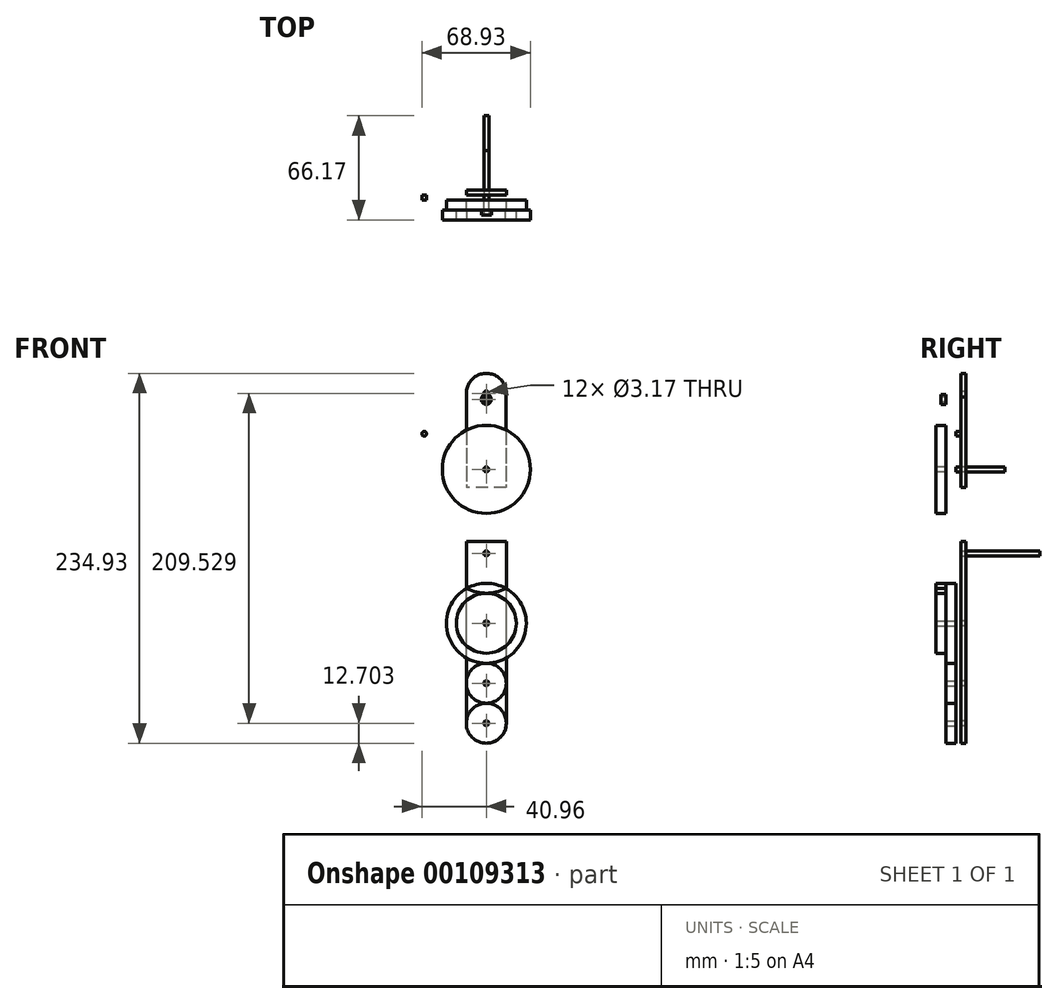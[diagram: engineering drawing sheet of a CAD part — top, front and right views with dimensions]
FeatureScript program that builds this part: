
annotation { "Feature Type Name" : "Feature", "Feature Type Description" : "" }
export const myFeature = defineFeature(function(context is Context, id is Id, definition is map)
    precondition{}
    {
        {
            var Q0;
            Q0=qCreatedBy(makeId("Front.planeOp"),FACE);
            var sketch = newSketch(context, id + "F0", { "sketchPlane" : qUnion([Q0])});
            skLineSegment(sketch, "E0.MirrorCS", {"start": v(12.47, 255.41) * mm, "end": v(42.64, 235.3) * mm});
            skArc(sketch, "E1.MirrorCS", {"start": v(12.47, 255.41) * mm, "mid": v(9.8, 265.9) * mm, "end": v(0, 270.52) * mm});
            skArc(sketch, "E2", {"start": v(-12.7, 48.29) * mm, "mid": v(0, 35.59) * mm, "end": v(12.7, 48.29) * mm});
            skLineSegment(sketch, "E3", {"start": v(12.7, 48.29) * mm, "end": v(42.64, 71.85) * mm});
            skLineSegment(sketch, "E4", {"start": v(42.64, 71.85) * mm, "end": v(42.64, 235.3) * mm});
            skLineSegment(sketch, "E5", {"start": v(-44.4, 144.8) * mm, "end": v(42.64, 144.8) * mm});
            skLineSegment(sketch, "E6", {"start": v(-44.4, 151.14) * mm, "end": v(-44.4, 144.8) * mm});
            skArc(sketch, "E7.MirrorCS", {"start": v(-12.47, 255.41) * mm, "mid": v(-9.8, 265.9) * mm, "end": v(0, 270.52) * mm});
            skLineSegment(sketch, "E8.MirrorCS", {"start": v(-12.47, 255.41) * mm, "end": v(-42.64, 235.3) * mm});
            skLineSegment(sketch, "E9.MirrorCS", {"start": v(-12.7, 48.29) * mm, "end": v(-42.64, 71.85) * mm});
            skLineSegment(sketch, "E10", {"start": v(-44.4, 144.8) * mm, "end": v(-42.64, 71.85) * mm});
            skLineSegment(sketch, "E11", {"start": v(-42.64, 235.3) * mm, "end": v(-44.4, 151.14) * mm});
            skLineSegment(sketch, "E12", {"start": v(42.64, 197.98) * mm, "end": v(-43.42, 197.98) * mm});
            skSolve(sketch);
        }
        {
            var Q0;
            Q0=makeQuery(id+"F0.imprint","IMPRINT",FACE,{"disambiguationData":[TD([[makeQuery(id+"F0.imprint","IMPRINT",EDGE,{"derivedFrom":sQuery(id+"F0.wireOp",EDGE,"E0.MirrorCS")}),-1.0]])]});
            var Q1;
            Q1=makeQuery(id+"F0.imprint","IMPRINT",FACE,{"disambiguationData":[TD([[makeQuery(id+"F0.imprint","IMPRINT",EDGE,{"derivedFrom":sQuery(id+"F0.wireOp",EDGE,"E2")}),1.0]])]});
            var Q2;
            {var subQ0=sQuery(id+"F0.wireOp",EDGE,"E5");Q2=makeQuery(id+"F0.imprint","IMPRINT",FACE,{"disambiguationData":[TD([[makeQuery(id+"F0.imprint","IMPRINT",EDGE,{"derivedFrom":subQ0}),1.0]])]});}
            extrude(context, id + "F1", {"entities" : qUnion([Q0, Q1, Q2]), "depth" : 3.17 * mm});
        }
        {
            var Q0;
            Q0=makeQuery(id+"F1.opExtrude","CAP_FACE",FACE,{"disambiguationData":[OSD([sQuery(id+"F0.wireOp",EDGE,"5b1c23d3-aa6b-4bc7-b0e1-dfea17c18ce91.MirrorCS"),sQuery(id+"F0.wireOp",EDGE,"5b1c23d3-aa6b-4bc7-b0e1-dfea17c18ce92.MirrorCS"),sQuery(id+"F0.wireOp",EDGE,"5b1c23d3-aa6b-4bc7-b0e1-dfea17c18ce95.MirrorCS"),sQuery(id+"F0.wireOp",EDGE,"0EXZE5XB-GXe8-Z4rD-Z6Uw-QY02pqgCHJHw"),sQuery(id+"F0.wireOp",EDGE,"aLZ1Et3P-EpBn-NYGt-KDQH-9Qiia9vVUrST"),sQuery(id+"F0.wireOp",EDGE,"E0.MirrorCS"),sQuery(id+"F0.wireOp",EDGE,"E1.MirrorCS"),sQuery(id+"F0.wireOp",EDGE,"58c32018-2fe2-45b1-866c-2011fd302cb82.MirrorCS"),sQuery(id+"F0.wireOp",EDGE,"58c32018-2fe2-45b1-866c-2011fd302cb83.MirrorCS"),sQuery(id+"F0.wireOp",EDGE,"58c32018-2fe2-45b1-866c-2011fd302cb84.MirrorCS")])],"isStart":false});
            var sketch = newSketch(context, id + "F2", { "sketchPlane" : qUnion([Q0])});
            skCircle(sketch, "E13", {"center": v(0, 254) * mm, "radius": 31.75 * mm});
            skLineSegment(sketch, "E14", {"start": v(0, 254) * mm, "end": v(0, 48.29) * mm, "construction": true});
            skSolve(sketch);
        }
        {
            var Q0;
            {var subQ5=makeQuery(id+"F1.opExtrude","CAP_EDGE",EDGE,{"disambiguationData":[OSD([sQuery(id+"F0.wireOp",EDGE,"E1.MirrorCS")])],"isStart":false});Q0=makeQuery(id+"F2.imprint","IMPRINT",FACE,{"disambiguationData":[TD([[makeQuery(id+"F2.imprint","IMPRINT",EDGE,{"derivedFrom":subQ5}),-1.0]])]});}
            var Q1;
            {var subQ5=makeQuery(id+"F1.opExtrude","CAP_EDGE",EDGE,{"disambiguationData":[OSD([sQuery(id+"F0.wireOp",EDGE,"E1.MirrorCS")])],"isStart":false});Q1=makeQuery(id+"F2.imprint","IMPRINT",FACE,{"disambiguationData":[TD([[makeQuery(id+"F2.imprint","IMPRINT",EDGE,{"derivedFrom":subQ5}),1.0]])]});}
            extrude(context, id + "F3", {"entities" : qUnion([Q0, Q1]), "depth" : 6.35 * mm});
        }
        {
            var Q0;
            Q0=makeQuery(id+"F1.opExtrude","CAP_FACE",FACE,{"disambiguationData":[OSD([sQuery(id+"F0.wireOp",EDGE,"5b1c23d3-aa6b-4bc7-b0e1-dfea17c18ce91.MirrorCS"),sQuery(id+"F0.wireOp",EDGE,"5b1c23d3-aa6b-4bc7-b0e1-dfea17c18ce92.MirrorCS"),sQuery(id+"F0.wireOp",EDGE,"5b1c23d3-aa6b-4bc7-b0e1-dfea17c18ce95.MirrorCS"),sQuery(id+"F0.wireOp",EDGE,"0EXZE5XB-GXe8-Z4rD-Z6Uw-QY02pqgCHJHw"),sQuery(id+"F0.wireOp",EDGE,"aLZ1Et3P-EpBn-NYGt-KDQH-9Qiia9vVUrST"),sQuery(id+"F0.wireOp",EDGE,"E0.MirrorCS"),sQuery(id+"F0.wireOp",EDGE,"E1.MirrorCS"),sQuery(id+"F0.wireOp",EDGE,"58c32018-2fe2-45b1-866c-2011fd302cb82.MirrorCS"),sQuery(id+"F0.wireOp",EDGE,"58c32018-2fe2-45b1-866c-2011fd302cb83.MirrorCS"),sQuery(id+"F0.wireOp",EDGE,"58c32018-2fe2-45b1-866c-2011fd302cb84.MirrorCS")])],"isStart":false});
            var sketch = newSketch(context, id + "F4", { "sketchPlane" : qUnion([Q0])});
            skCircle(sketch, "E15", {"center": v(0, 209.55) * mm, "radius": 12.7 * mm});
            skSolve(sketch);
        }
        {
            var Q0;
            Q0=makeQuery(id+"F4.imprint","IMPRINT",FACE,{"disambiguationData":[TD([[makeQuery(id+"F4.imprint","IMPRINT",EDGE,{"derivedFrom":sQuery(id+"F4.wireOp",EDGE,"E15")}),1.0]])]});
            extrude(context, id + "F5", {"entities" : qUnion([Q0]), "depth" : 6.35 * mm});
        }
        {
            var Q0;
            Q0=makeQuery(id+"F5.opExtrude","CAP_FACE",FACE,{"disambiguationData":[OSD([sQuery(id+"F4.wireOp",EDGE,"E15")])],"isStart":false});
            var sketch = newSketch(context, id + "F6", { "sketchPlane" : qUnion([Q0])});
            skCircle(sketch, "E16", {"center": v(0, 209.55) * mm, "radius": 40.64 * mm});
            skSolve(sketch);
        }
        {
            var Q0;
            Q0=makeQuery(id+"F6.imprint","IMPRINT",FACE,{"disambiguationData":[TD([[makeQuery(id+"F6.imprint","IMPRINT",EDGE,{"derivedFrom":sQuery(id+"F6.wireOp",EDGE,"E16")}),1.0]])]});
            var Q1;
            Q1=makeQuery(id+"F6.imprint","IMPRINT",FACE,{"disambiguationData":[TD([[makeQuery(id+"F6.imprint","IMPRINT",EDGE,{"derivedFrom":makeQuery(id+"F5.opExtrude","CAP_EDGE",EDGE,{"disambiguationData":[OSD([sQuery(id+"F4.wireOp",EDGE,"E15")])],"isStart":false})}),1.0]])]});
            extrude(context, id + "F7", {"entities" : qUnion([Q0, Q1]), "depth" : 6.35 * mm});
        }
        {
            var Q0;
            Q0=makeQuery(id+"F7.opExtrude","CAP_FACE",FACE,{"disambiguationData":[OSD([sQuery(id+"F6.wireOp",EDGE,"E16")])],"isStart":true});
            var sketch = newSketch(context, id + "F8", { "sketchPlane" : qUnion([Q0])});
            skCircle(sketch, "E17", {"center": v(0, 156.21) * mm, "radius": 12.7 * mm});
            skSolve(sketch);
        }
        {
            var Q0;
            Q0=makeQuery(id+"F8.imprint","IMPRINT",FACE,{"disambiguationData":[TD([[makeQuery(id+"F8.imprint","IMPRINT",EDGE,{"derivedFrom":sQuery(id+"F8.wireOp",EDGE,"E17")}),1.0]])]});
            extrude(context, id + "F9", {"entities" : qUnion([Q0]), "oppositeDirection" : true, "depth" : 6.35 * mm});
        }
        {
            var Q0;
            Q0=makeQuery(id+"F9.opExtrude","CAP_FACE",FACE,{"disambiguationData":[OSD([sQuery(id+"F8.wireOp",EDGE,"E17")])],"isStart":true});
            var sketch = newSketch(context, id + "F10", { "sketchPlane" : qUnion([Q0])});
            skCircle(sketch, "E18", {"center": v(0, 156.21) * mm, "radius": 31.75 * mm});
            skSolve(sketch);
        }
        {
            var Q0;
            Q0=qSketchRegion(id+"F10",true);
            extrude(context, id + "F11", {"entities" : qUnion([Q0]), "depth" : 6.35 * mm});
        }
        {
            var Q0;
            Q0=makeQuery(id+"F1.opExtrude","CAP_FACE",FACE,{"disambiguationData":[OSD([sQuery(id+"F0.wireOp",EDGE,"5b1c23d3-aa6b-4bc7-b0e1-dfea17c18ce91.MirrorCS"),sQuery(id+"F0.wireOp",EDGE,"5b1c23d3-aa6b-4bc7-b0e1-dfea17c18ce92.MirrorCS"),sQuery(id+"F0.wireOp",EDGE,"5b1c23d3-aa6b-4bc7-b0e1-dfea17c18ce95.MirrorCS"),sQuery(id+"F0.wireOp",EDGE,"0EXZE5XB-GXe8-Z4rD-Z6Uw-QY02pqgCHJHw"),sQuery(id+"F0.wireOp",EDGE,"aLZ1Et3P-EpBn-NYGt-KDQH-9Qiia9vVUrST"),sQuery(id+"F0.wireOp",EDGE,"E0.MirrorCS"),sQuery(id+"F0.wireOp",EDGE,"E1.MirrorCS"),sQuery(id+"F0.wireOp",EDGE,"58c32018-2fe2-45b1-866c-2011fd302cb82.MirrorCS"),sQuery(id+"F0.wireOp",EDGE,"58c32018-2fe2-45b1-866c-2011fd302cb83.MirrorCS"),sQuery(id+"F0.wireOp",EDGE,"58c32018-2fe2-45b1-866c-2011fd302cb84.MirrorCS")])],"isStart":false});
            var sketch = newSketch(context, id + "F12", { "sketchPlane" : qUnion([Q0])});
            skCircle(sketch, "E19", {"center": v(0, 111.76) * mm, "radius": 12.7 * mm});
            skSolve(sketch);
        }
        {
            var Q0;
            Q0=makeQuery(id+"F12.imprint","IMPRINT",FACE,{"disambiguationData":[TD([[makeQuery(id+"F12.imprint","IMPRINT",EDGE,{"derivedFrom":sQuery(id+"F12.wireOp",EDGE,"E19")}),1.0]])]});
            extrude(context, id + "F13", {"entities" : qUnion([Q0]), "depth" : 6.35 * mm});
        }
        {
            var Q0;
            Q0=makeQuery(id+"F13.opExtrude","CAP_FACE",FACE,{"disambiguationData":[OSD([sQuery(id+"F12.wireOp",EDGE,"E19")])],"isStart":false});
            var sketch = newSketch(context, id + "F14", { "sketchPlane" : qUnion([Q0])});
            skCircle(sketch, "E20", {"center": v(0, 111.8) * mm, "radius": 25.4 * mm});
            skSolve(sketch);
        }
        {
            var Q0;
            Q0=qSketchRegion(id+"F14",true);
            extrude(context, id + "F15", {"entities" : qUnion([Q0]), "depth" : 6.35 * mm});
        }
        {
            var Q0;
            Q0=makeQuery(id+"F15.opExtrude","CAP_FACE",FACE,{"disambiguationData":[OSD([sQuery(id+"F14.wireOp",EDGE,"E20")])],"isStart":true});
            var sketch = newSketch(context, id + "F16", { "sketchPlane" : qUnion([Q0])});
            skCircle(sketch, "E21", {"center": v(0, 73.7) * mm, "radius": 12.7 * mm});
            skSolve(sketch);
        }
        {
            var Q0;
            Q0=makeQuery(id+"F16.imprint","IMPRINT",FACE,{"disambiguationData":[TD([[makeQuery(id+"F16.imprint","IMPRINT",EDGE,{"derivedFrom":sQuery(id+"F16.wireOp",EDGE,"E21")}),1.0]])]});
            extrude(context, id + "F17", {"entities" : qUnion([Q0]), "oppositeDirection" : true, "depth" : 6.35 * mm});
        }
        {
            var Q0;
            Q0=makeQuery(id+"F17.opExtrude","CAP_FACE",FACE,{"disambiguationData":[OSD([sQuery(id+"F16.wireOp",EDGE,"E21")])],"isStart":false});
            var sketch = newSketch(context, id + "F18", { "sketchPlane" : qUnion([Q0])});
            skCircle(sketch, "E22", {"center": v(0, 48.3) * mm, "radius": 12.7 * mm});
            skSolve(sketch);
        }
        {
            var Q0;
            Q0=makeQuery(id+"F18.imprint","IMPRINT",FACE,{"disambiguationData":[TD([[makeQuery(id+"F18.imprint","IMPRINT",EDGE,{"derivedFrom":sQuery(id+"F18.wireOp",EDGE,"E22")}),1.0]])]});
            extrude(context, id + "F19", {"entities" : qUnion([Q0]), "oppositeDirection" : true, "depth" : 6.35 * mm});
        }
        {
            var Q0;
            Q0=makeQuery(id+"F3.opExtrude","CAP_FACE",FACE,{"disambiguationData":[OSD([sQuery(id+"F2.wireOp",EDGE,"E13")])],"isStart":false});
            var sketch = newSketch(context, id + "F20", { "sketchPlane" : qUnion([Q0])});
            skCircle(sketch, "E23", {"center": v(0, 254) * mm, "radius": 3.18 * mm});
            skSolve(sketch);
        }
        {
            var Q0;
            Q0=makeQuery(id+"F20.imprint","IMPRINT",FACE,{"disambiguationData":[TD([[makeQuery(id+"F20.imprint","IMPRINT",EDGE,{"derivedFrom":sQuery(id+"F20.wireOp",EDGE,"E23")}),1.0]])]});
            extrude(context, id + "F21", {"entities" : qUnion([Q0]), "depth" : 3.17 * mm});
        }
        {
            var Q0;
            {var subQ3=sQuery(id+"F0.wireOp",EDGE,"E0.MirrorCS");Q0=makeQuery(id+"F0.imprint","IMPRINT",FACE,{"disambiguationData":[TD([[makeQuery(id+"F0.imprint","IMPRINT",EDGE,{"derivedFrom":subQ3}),-1.0]])]});}
            var Q1;
            Q1=makeQuery(id+"F0.imprint","IMPRINT",FACE,{"disambiguationData":[TD([[makeQuery(id+"F0.imprint","IMPRINT",EDGE,{"derivedFrom":sQuery(id+"F0.wireOp",EDGE,"E2")}),1.0]])]});
            extrude(context, id + "F22", {"entities" : qUnion([Q0, Q1]), "oppositeDirection" : true, "depth" : 3.17 * mm});
        }
        {
            var Q0;
            Q0=makeQuery(id+"F7.opExtrude","CAP_FACE",FACE,{"disambiguationData":[OSD([sQuery(id+"F6.wireOp",EDGE,"E16")])],"isStart":false});
            var sketch = newSketch(context, id + "F23", { "sketchPlane" : qUnion([Q0])});
            skCircle(sketch, "E24", {"center": v(0, 209.55) * mm, "radius": 1.59 * mm});
            skCircle(sketch, "E25", {"center": v(0, 156.21) * mm, "radius": 1.59 * mm});
            skCircle(sketch, "E26", {"center": v(0, 111.8) * mm, "radius": 1.59 * mm});
            skCircle(sketch, "E27", {"center": v(0, 73.7) * mm, "radius": 1.59 * mm});
            skCircle(sketch, "E28", {"center": v(0, 48.3) * mm, "radius": 1.59 * mm});
            skSolve(sketch);
        }
        {
            var Q0;
            Q0=qSketchRegion(id+"F23",true);
            var Q1;
            Q1=makeQuery(id+"F22.opExtrude","CAP_FACE",FACE,{"disambiguationData":[OSD([sQuery(id+"F0.wireOp",EDGE,"E0.MirrorCS"),sQuery(id+"F0.wireOp",EDGE,"E1.MirrorCS"),sQuery(id+"F0.wireOp",EDGE,"58c32018-2fe2-45b1-866c-2011fd302cb82.MirrorCS"),sQuery(id+"F0.wireOp",EDGE,"oskGFAkM-XsRB-bvMx-Ji8E-cj2Pl0QT4DN1"),sQuery(id+"F0.wireOp",EDGE,"E4"),sQuery(id+"F0.wireOp",EDGE,"0CljIG2g-A6Mw-YOEX-ZIKO-MWRqugUd6cpU")])],"isStart":false});
            extrude(context, id + "F24", {"entities" : qUnion([Q0]), "operationType" : NewBodyOperationType.REMOVE, "endBound" : BoundingType.THROUGH_ALL, "oppositeDirection" : true, "endBoundEntityFace" : qUnion([Q1]), "depth" : 56.1 * mm});
        }
        {
            var Q0;
            Q0=makeQuery(id+"F23.imprint","IMPRINT",FACE,{"disambiguationData":[TD([[makeQuery(id+"F23.imprint","IMPRINT",EDGE,{"derivedFrom":sQuery(id+"F23.wireOp",EDGE,"E25")}),1.0]])]});
            extrude(context, id + "F25", {"entities" : qUnion([Q0]), "oppositeDirection" : true, "depth" : 57.15 * mm + 9 * mm + 2 / 203.2 * mm + 2 / 203.2 * mm});
        }
        {
            var Q0;
            Q0=makeQuery(id+"F23.imprint","IMPRINT",FACE,{"disambiguationData":[TD([[makeQuery(id+"F23.imprint","IMPRINT",EDGE,{"derivedFrom":sQuery(id+"F23.wireOp",EDGE,"E24")}),1.0]])]});
            extrude(context, id + "F26", {"entities" : qUnion([Q0]), "oppositeDirection" : true, "depth" : 34.92 * mm + 9 * mm + 2 / 203.2 * mm});
        }
        {
            var Q0;
            Q0=makeQuery(id+"F21.opExtrude","CAP_FACE",FACE,{"disambiguationData":[OSD([sQuery(id+"F20.wireOp",EDGE,"E23")])],"isStart":false});
            var sketch = newSketch(context, id + "F27", { "sketchPlane" : qUnion([Q0])});
            skCircle(sketch, "E29", {"center": v(0, 254) * mm, "radius": 1.59 * mm});
            skSolve(sketch);
        }
        {
            var Q0;
            Q0=makeQuery(id+"F27.imprint","IMPRINT",FACE,{"disambiguationData":[TD([[makeQuery(id+"F27.imprint","IMPRINT",EDGE,{"derivedFrom":sQuery(id+"F27.wireOp",EDGE,"E29")}),1.0]])]});
            extrude(context, id + "F28", {"entities" : qUnion([Q0]), "operationType" : NewBodyOperationType.REMOVE, "oppositeDirection" : true, "depth" : 9.52 * mm});
        }
        {
            var Q0;
            Q0=makeQuery(id+"F22.opExtrude","CAP_FACE",FACE,{"disambiguationData":[OSD([sQuery(id+"F0.wireOp",EDGE,"E0.MirrorCS"),sQuery(id+"F0.wireOp",EDGE,"E1.MirrorCS"),sQuery(id+"F0.wireOp",EDGE,"E4"),sQuery(id+"F0.wireOp",EDGE,"0CljIG2g-A6Mw-YOEX-ZIKO-MWRqugUd6cpU"),sQuery(id+"F0.wireOp",EDGE,"E7.MirrorCS"),sQuery(id+"F0.wireOp",EDGE,"E8.MirrorCS"),sQuery(id+"F0.wireOp",EDGE,"E11")])],"isStart":false});
            var sketch = newSketch(context, id + "F29", { "sketchPlane" : qUnion([Q0])});
            skCircle(sketch, "E30", {"center": v(0, 257.82) * mm, "radius": 1.59 * mm});
            skSolve(sketch);
        }
        {
            var Q0;
            Q0=qSketchRegion(id+"F29",true);
            extrude(context, id + "F30", {"entities" : qUnion([Q0]), "operationType" : NewBodyOperationType.REMOVE, "oppositeDirection" : true, "depth" : 6.35 * mm});
        }
        {
            var Q0;
            Q0=makeQuery(id+"F22.opExtrude","CAP_FACE",FACE,{"disambiguationData":[OSD([sQuery(id+"F0.wireOp",EDGE,"E0.MirrorCS"),sQuery(id+"F0.wireOp",EDGE,"E1.MirrorCS"),sQuery(id+"F0.wireOp",EDGE,"E4"),sQuery(id+"F0.wireOp",EDGE,"0CljIG2g-A6Mw-YOEX-ZIKO-MWRqugUd6cpU"),sQuery(id+"F0.wireOp",EDGE,"E7.MirrorCS"),sQuery(id+"F0.wireOp",EDGE,"E8.MirrorCS"),sQuery(id+"F0.wireOp",EDGE,"E11")])],"isStart":false});
            var sketch = newSketch(context, id + "F31", { "sketchPlane" : qUnion([Q0])});
            skLineSegment(sketch, "E31", {"start": v(-12.47, 255.41) * mm, "end": v(-12.47, 151.14) * mm});
            skLineSegment(sketch, "E32", {"start": v(12.47, 255.41) * mm, "end": v(12.47, 151.14) * mm});
            skSolve(sketch);
        }
        {
            var Q0;
            {var subQ0=sQuery(id+"F31.wireOp",EDGE,"E31");Q0=makeQuery(id+"F31.imprint","IMPRINT",FACE,{"disambiguationData":[TD([[makeQuery(id+"F31.imprint","IMPRINT",EDGE,{"derivedFrom":subQ0}),-1.0]])]});}
            var Q1;
            {var subQ0=sQuery(id+"F31.wireOp",EDGE,"E32");Q1=makeQuery(id+"F31.imprint","IMPRINT",FACE,{"disambiguationData":[TD([[makeQuery(id+"F31.imprint","IMPRINT",EDGE,{"derivedFrom":subQ0}),1.0]])]});}
            extrude(context, id + "F32", {"entities" : qUnion([Q0, Q1]), "operationType" : NewBodyOperationType.REMOVE, "oppositeDirection" : true, "depth" : 3.17 * mm});
        }
        {
            var Q0;
            Q0=makeQuery(id+"F22.opExtrude","CAP_FACE",FACE,{"disambiguationData":[OSD([sQuery(id+"F0.wireOp",EDGE,"E2"),sQuery(id+"F0.wireOp",EDGE,"E3"),sQuery(id+"F0.wireOp",EDGE,"E4"),sQuery(id+"F0.wireOp",EDGE,"E5"),sQuery(id+"F0.wireOp",EDGE,"E9.MirrorCS"),sQuery(id+"F0.wireOp",EDGE,"E10")])],"isStart":false});
            var sketch = newSketch(context, id + "F33", { "sketchPlane" : qUnion([Q0])});
            skLineSegment(sketch, "E33", {"start": v(-12.7, 48.29) * mm, "end": v(-12.7, 144.8) * mm});
            skLineSegment(sketch, "E34", {"start": v(12.7, 48.29) * mm, "end": v(12.7, 144.8) * mm});
            skSolve(sketch);
        }
        {
            var Q0;
            {var subQ0=sQuery(id+"F33.wireOp",EDGE,"E33");Q0=makeQuery(id+"F33.imprint","IMPRINT",FACE,{"disambiguationData":[TD([[makeQuery(id+"F33.imprint","IMPRINT",EDGE,{"derivedFrom":subQ0}),1.0]])]});}
            var Q1;
            {var subQ0=sQuery(id+"F33.wireOp",EDGE,"E34");Q1=makeQuery(id+"F33.imprint","IMPRINT",FACE,{"disambiguationData":[TD([[makeQuery(id+"F33.imprint","IMPRINT",EDGE,{"derivedFrom":subQ0}),-1.0]])]});}
            extrude(context, id + "F34", {"entities" : qUnion([Q0, Q1]), "operationType" : NewBodyOperationType.REMOVE, "oppositeDirection" : true, "depth" : 3.17 * mm});
        }
        {
            var Q0;
            Q0=makeQuery(id+"F22.opExtrude","SWEPT_FACE",FACE,{"disambiguationData":[OSD([sQuery(id+"F0.wireOp",EDGE,"E5")])]});
            extrude(context, id + "F35", {"entities" : qUnion([Q0]), "operationType" : NewBodyOperationType.ADD, "depth" : 19.05 * mm});
        }
        {
            var Q0;
            {var subQ0=sQuery(id+"F0.wireOp",EDGE,"E5");Q0=makeQuery(id+"F35.boolean.opBoolean","MERGE",FACE,{"derivedFrom":[makeQuery(id+"F22.opExtrude","CAP_FACE",FACE,{"disambiguationData":[OSD([sQuery(id+"F0.wireOp",EDGE,"E2"),sQuery(id+"F0.wireOp",EDGE,"E3"),sQuery(id+"F0.wireOp",EDGE,"E4"),subQ0,sQuery(id+"F0.wireOp",EDGE,"E9.MirrorCS"),sQuery(id+"F0.wireOp",EDGE,"E10")])],"isStart":false}),makeQuery(id+"F35.opExtrude","SWEPT_FACE",FACE,{"disambiguationData":[OSD([subQ0]),TDD([makeQuery(id+"F22.opExtrude","CAP_EDGE",EDGE,{"disambiguationData":[OSD([subQ0])],"isStart":false})])]})]});}
            var sketch = newSketch(context, id + "F36", { "sketchPlane" : qUnion([Q0])});
            skCircle(sketch, "E35.0", {"center": v(0, 156.21) * mm, "radius": 1.59 * mm});
            skSolve(sketch);
        }
        {
            var Q0;
            Q0=qSketchRegion(id+"F36",true);
            extrude(context, id + "F37", {"entities" : qUnion([Q0]), "operationType" : NewBodyOperationType.REMOVE, "oppositeDirection" : true, "depth" : 3.17 * mm});
        }
        {
            var Q0;
            Q0=makeQuery(id+"F1.opExtrude","CAP_FACE",FACE,{"disambiguationData":[OSD([sQuery(id+"F0.wireOp",EDGE,"E0.MirrorCS"),sQuery(id+"F0.wireOp",EDGE,"E1.MirrorCS"),sQuery(id+"F0.wireOp",EDGE,"E2"),sQuery(id+"F0.wireOp",EDGE,"E3"),sQuery(id+"F0.wireOp",EDGE,"E4"),sQuery(id+"F0.wireOp",EDGE,"E6"),sQuery(id+"F0.wireOp",EDGE,"E7.MirrorCS"),sQuery(id+"F0.wireOp",EDGE,"E8.MirrorCS"),sQuery(id+"F0.wireOp",EDGE,"E9.MirrorCS"),sQuery(id+"F0.wireOp",EDGE,"E10"),sQuery(id+"F0.wireOp",EDGE,"E11")])],"isStart":false});
            var sketch = newSketch(context, id + "F38", { "sketchPlane" : qUnion([Q0])});
            skCircle(sketch, "E36", {"center": v(0, 48.3) * mm, "radius": 12.7 * mm});
            skCircle(sketch, "E37", {"center": v(0, 73.7) * mm, "radius": 12.7 * mm});
            skCircle(sketch, "E38", {"center": v(0, 111.8) * mm, "radius": 25.4 * mm});
            skSolve(sketch);
        }
        {
            var Q0;
            Q0=makeQuery(id+"F38.imprint","IMPRINT",FACE,{"disambiguationData":[TD([[makeQuery(id+"F38.imprint","IMPRINT",EDGE,{"derivedFrom":sQuery(id+"F38.wireOp",EDGE,"E38")}),1.0]])]});
            var Q1;
            {var subQ0=sQuery(id+"F38.wireOp",EDGE,"E37");var subQ1=makeQuery(id+"F38.imprint","INTERSECT",VERTEX,{"derivedFrom":[sQuery(id+"F38.wireOp",EDGE,"E36"),subQ0]});Q1=makeQuery(id+"F38.imprint","IMPRINT",FACE,{"disambiguationData":[TD([[makeQuery(id+"F38.imprint","IMPRINT",EDGE,{"disambiguationData":[TD([[subQ1,1.0]])],"derivedFrom":subQ0}),1.0]])]});}
            var Q2;
            {var subQ0=sQuery(id+"F38.wireOp",EDGE,"E36");var subQ5=makeQuery(id+"F38.imprint","INTERSECT",VERTEX,{"derivedFrom":[subQ0,sQuery(id+"F38.wireOp",EDGE,"E37")]});Q2=makeQuery(id+"F38.imprint","IMPRINT",FACE,{"disambiguationData":[TD([[makeQuery(id+"F38.imprint","IMPRINT",EDGE,{"disambiguationData":[TD([[subQ5,-1.0]])],"derivedFrom":subQ0}),1.0]])]});}
            extrude(context, id + "F39", {"entities" : qUnion([Q0, Q1, Q2]), "depth" : 6.35 * mm});
        }
        {
            var Q0;
            Q0=makeQuery(id+"F39.opExtrude","CAP_FACE",FACE,{"disambiguationData":[OSD([sQuery(id+"F0.wireOp",EDGE,"E0.MirrorCS"),sQuery(id+"F0.wireOp",EDGE,"E1.MirrorCS"),sQuery(id+"F0.wireOp",EDGE,"E2"),sQuery(id+"F0.wireOp",EDGE,"E3"),sQuery(id+"F0.wireOp",EDGE,"E4"),sQuery(id+"F0.wireOp",EDGE,"E6"),sQuery(id+"F0.wireOp",EDGE,"E7.MirrorCS"),sQuery(id+"F0.wireOp",EDGE,"E8.MirrorCS"),sQuery(id+"F0.wireOp",EDGE,"E9.MirrorCS"),sQuery(id+"F0.wireOp",EDGE,"E10"),sQuery(id+"F0.wireOp",EDGE,"E11"),sQuery(id+"F23.wireOp",EDGE,"E26"),sQuery(id+"F38.wireOp",EDGE,"E38")])],"isStart":false});
            var sketch = newSketch(context, id + "F40", { "sketchPlane" : qUnion([Q0])});
            skCircle(sketch, "E39", {"center": v(0, 111.8) * mm, "radius": 19.05 * mm});
            skCircle(sketch, "E40.0", {"center": v(0, 156.21) * mm, "radius": 1.59 * mm, "construction": true});
            skCircle(sketch, "E41", {"center": v(0, 156.21) * mm, "radius": 25.37 * mm});
            skCircle(sketch, "E42", {"center": v(0, 209.55) * mm, "radius": 27.97 * mm});
            skSolve(sketch);
        }
        {
            var Q0;
            Q0=makeQuery(id+"F40.imprint","IMPRINT",FACE,{"disambiguationData":[TD([[makeQuery(id+"F40.imprint","IMPRINT",EDGE,{"derivedFrom":sQuery(id+"F40.wireOp",EDGE,"E39")}),1.0]])]});
            var Q1;
            {var subQ0=sQuery(id+"F40.wireOp",EDGE,"E41");var subQ1=makeQuery(id+"F39.opExtrude","CAP_EDGE",EDGE,{"disambiguationData":[OSD([sQuery(id+"F38.wireOp",EDGE,"E38")])],"isStart":false});var subQ2=makeQuery(id+"F40.imprint","INTERSECT",VERTEX,{"disambiguationData":[OD(0.0)],"derivedFrom":[subQ1,subQ0]});Q1=makeQuery(id+"F40.imprint","IMPRINT",FACE,{"disambiguationData":[TD([[makeQuery(id+"F40.imprint","IMPRINT",EDGE,{"disambiguationData":[TD([[subQ2,1.0]])],"derivedFrom":subQ0}),1.0]])]});}
            var Q2;
            {var subQ0=sQuery(id+"F40.wireOp",EDGE,"E41");var subQ1=makeQuery(id+"F40.imprint","INTERSECT",VERTEX,{"derivedFrom":[sQuery(id+"F40.wireOp",EDGE,"E39"),subQ0]});Q2=makeQuery(id+"F40.imprint","IMPRINT",FACE,{"disambiguationData":[TD([[makeQuery(id+"F40.imprint","IMPRINT",EDGE,{"disambiguationData":[TD([[subQ1,1.0]])],"derivedFrom":subQ0}),1.0]])]});}
            var Q3;
            Q3=makeQuery(id+"F40.imprint","IMPRINT",FACE,{"disambiguationData":[TD([[makeQuery(id+"F40.imprint","IMPRINT",EDGE,{"derivedFrom":sQuery(id+"F40.wireOp",EDGE,"E42")}),1.0]])]});
            extrude(context, id + "F41", {"entities" : qUnion([Q0, Q1, Q2, Q3]), "depth" : 6.35 * mm});
        }
        {
            var Q0;
            Q0=makeQuery(id+"F41.opExtrude","CAP_FACE",FACE,{"disambiguationData":[OSD([sQuery(id+"F40.wireOp",EDGE,"E42")])],"isStart":false});
            var sketch = newSketch(context, id + "F42", { "sketchPlane" : qUnion([Q0])});
            skCircle(sketch, "E43", {"center": v(0, 209.55) * mm, "radius": 1.59 * mm});
            skCircle(sketch, "E44", {"center": v(0, 156.21) * mm, "radius": 1.59 * mm});
            skSolve(sketch);
        }
        {
            var Q0;
            Q0=makeQuery(id+"F42.imprint","IMPRINT",FACE,{"disambiguationData":[TD([[makeQuery(id+"F42.imprint","IMPRINT",EDGE,{"derivedFrom":sQuery(id+"F42.wireOp",EDGE,"E43")}),1.0]])]});
            var Q1;
            Q1=makeQuery(id+"F42.imprint","IMPRINT",FACE,{"disambiguationData":[TD([[makeQuery(id+"F42.imprint","IMPRINT",EDGE,{"derivedFrom":sQuery(id+"F42.wireOp",EDGE,"E44")}),1.0]])]});
            extrude(context, id + "F43", {"entities" : qUnion([Q0, Q1]), "operationType" : NewBodyOperationType.REMOVE, "oppositeDirection" : true, "depth" : 12.7 * mm});
        }
        {
            var Q0;
            Q0=makeQuery(id+"F3.opExtrude","SWEPT_BODY",BODY,{"disambiguationData":[OSD([sQuery(id+"F2.wireOp",EDGE,"E13")])]});
            var Q1;
            Q1=makeQuery(id+"F7.opExtrude","SWEPT_BODY",BODY,{"disambiguationData":[OSD([sQuery(id+"F6.wireOp",EDGE,"E16")])]});
            var Q2;
            Q2=makeQuery(id+"F11.opExtrude","SWEPT_BODY",BODY,{"disambiguationData":[OSD([sQuery(id+"F10.wireOp",EDGE,"E18")])]});
            var Q3;
            Q3=makeQuery(id+"F5.opExtrude","SWEPT_BODY",BODY,{"disambiguationData":[OSD([sQuery(id+"F4.wireOp",EDGE,"E15")])]});
            var Q4;
            Q4=makeQuery(id+"F13.opExtrude","SWEPT_BODY",BODY,{"disambiguationData":[OSD([sQuery(id+"F12.wireOp",EDGE,"E19")])]});
            var Q5;
            Q5=makeQuery(id+"F9.opExtrude","SWEPT_BODY",BODY,{"disambiguationData":[OSD([sQuery(id+"F8.wireOp",EDGE,"E17")])]});
            var Q6;
            Q6=makeQuery(id+"F17.opExtrude","SWEPT_BODY",BODY,{"disambiguationData":[OSD([sQuery(id+"F16.wireOp",EDGE,"E21")])]});
            var Q7;
            Q7=makeQuery(id+"F19.opExtrude","SWEPT_BODY",BODY,{"disambiguationData":[OSD([sQuery(id+"F18.wireOp",EDGE,"E22")])]});
            var Q8;
            Q8=makeQuery(id+"F15.opExtrude","SWEPT_BODY",BODY,{"disambiguationData":[OSD([sQuery(id+"F14.wireOp",EDGE,"E20")])]});
            deleteBodies(context, id + "F44", {"entities" : qUnion([Q0, Q1, Q2, Q3, Q4, Q5, Q6, Q7, Q8])});
        }
        {
            var Q0;
            Q0=makeQuery(id+"F1.opExtrude","CAP_FACE",FACE,{"disambiguationData":[OSD([sQuery(id+"F0.wireOp",EDGE,"E0.MirrorCS"),sQuery(id+"F0.wireOp",EDGE,"E1.MirrorCS"),sQuery(id+"F0.wireOp",EDGE,"E2"),sQuery(id+"F0.wireOp",EDGE,"E3"),sQuery(id+"F0.wireOp",EDGE,"E4"),sQuery(id+"F0.wireOp",EDGE,"E6"),sQuery(id+"F0.wireOp",EDGE,"E7.MirrorCS"),sQuery(id+"F0.wireOp",EDGE,"E8.MirrorCS"),sQuery(id+"F0.wireOp",EDGE,"E9.MirrorCS"),sQuery(id+"F0.wireOp",EDGE,"E10"),sQuery(id+"F0.wireOp",EDGE,"E11")])],"isStart":false});
            var sketch = newSketch(context, id + "F45", { "sketchPlane" : qUnion([Q0])});
            skLineSegment(sketch, "E45", {"start": v(-42.64, 235.3) * mm, "end": v(42.64, 235.3) * mm, "construction": true});
            skLineSegment(sketch, "E46", {"start": v(42.64, 232.12) * mm, "end": v(-42.7, 232.13) * mm, "construction": true});
            skLineSegment(sketch, "E47", {"start": v(42.64, 232.12) * mm, "end": v(39.46, 232.12) * mm, "construction": true});
            skCircle(sketch, "E48", {"center": v(39.46, 232.12) * mm, "radius": 1.5 * mm});
            skLineSegment(sketch, "E49", {"start": v(0, 257.82) * mm, "end": v(0, 46.7) * mm, "construction": true});
            skCircle(sketch, "E50.MirrorC", {"center": v(-39.46, 232.12) * mm, "radius": 1.5 * mm});
            skLineSegment(sketch, "E51", {"start": v(-42.64, 71.85) * mm, "end": v(42.64, 73.92) * mm, "construction": true});
            skLineSegment(sketch, "E52", {"start": v(-42.71, 75.03) * mm, "end": v(42.64, 77.1) * mm, "construction": true});
            skLineSegment(sketch, "E53", {"start": v(42.64, 77.1) * mm, "end": v(39.46, 77.01) * mm, "construction": true});
            skCircle(sketch, "E54", {"center": v(39.46, 77.01) * mm, "radius": 1.5 * mm});
            skLineSegment(sketch, "E55", {"start": v(-42.71, 75.03) * mm, "end": v(-39.54, 75.1) * mm, "construction": true});
            skCircle(sketch, "E56", {"center": v(-39.54, 75.1) * mm, "radius": 1.5 * mm});
            skLineSegment(sketch, "E57", {"start": v(-44.4, 151.14) * mm, "end": v(42.64, 151.14) * mm, "construction": true});
            skLineSegment(sketch, "E58", {"start": v(42.64, 151.14) * mm, "end": v(39.46, 151.14) * mm, "construction": true});
            skLineSegment(sketch, "E59", {"start": v(-44.4, 151.14) * mm, "end": v(-41.23, 151.14) * mm, "construction": true});
            skCircle(sketch, "E60", {"center": v(-41.23, 151.14) * mm, "radius": 1.5 * mm});
            skCircle(sketch, "E61", {"center": v(39.46, 151.14) * mm, "radius": 1.5 * mm});
            skSolve(sketch);
        }
        {
            var Q0;
            Q0=makeQuery(id+"F45.imprint","IMPRINT",FACE,{"disambiguationData":[TD([[makeQuery(id+"F45.imprint","IMPRINT",EDGE,{"derivedFrom":sQuery(id+"F45.wireOp",EDGE,"E48")}),1.0]])]});
            var Q1;
            Q1=makeQuery(id+"F45.imprint","IMPRINT",FACE,{"disambiguationData":[TD([[makeQuery(id+"F45.imprint","IMPRINT",EDGE,{"derivedFrom":sQuery(id+"F45.wireOp",EDGE,"E50.MirrorC")}),-1.0]])]});
            var Q2;
            Q2=makeQuery(id+"F45.imprint","IMPRINT",FACE,{"disambiguationData":[TD([[makeQuery(id+"F45.imprint","IMPRINT",EDGE,{"derivedFrom":sQuery(id+"F45.wireOp",EDGE,"E56")}),1.0]])]});
            var Q3;
            Q3=makeQuery(id+"F45.imprint","IMPRINT",FACE,{"disambiguationData":[TD([[makeQuery(id+"F45.imprint","IMPRINT",EDGE,{"derivedFrom":sQuery(id+"F45.wireOp",EDGE,"E54")}),1.0]])]});
            var Q4;
            Q4=makeQuery(id+"F45.imprint","IMPRINT",FACE,{"disambiguationData":[TD([[makeQuery(id+"F45.imprint","IMPRINT",EDGE,{"derivedFrom":sQuery(id+"F45.wireOp",EDGE,"E60")}),1.0]])]});
            var Q5;
            Q5=makeQuery(id+"F45.imprint","IMPRINT",FACE,{"disambiguationData":[TD([[makeQuery(id+"F45.imprint","IMPRINT",EDGE,{"derivedFrom":sQuery(id+"F45.wireOp",EDGE,"E61")}),1.0]])]});
            var Q6;
            Q6=makeQuery(id+"F1.opExtrude","CAP_FACE",FACE,{"disambiguationData":[OSD([sQuery(id+"F0.wireOp",EDGE,"E0.MirrorCS"),sQuery(id+"F0.wireOp",EDGE,"E1.MirrorCS"),sQuery(id+"F0.wireOp",EDGE,"E2"),sQuery(id+"F0.wireOp",EDGE,"E3"),sQuery(id+"F0.wireOp",EDGE,"E4"),sQuery(id+"F0.wireOp",EDGE,"E6"),sQuery(id+"F0.wireOp",EDGE,"E7.MirrorCS"),sQuery(id+"F0.wireOp",EDGE,"E8.MirrorCS"),sQuery(id+"F0.wireOp",EDGE,"E9.MirrorCS"),sQuery(id+"F0.wireOp",EDGE,"E10"),sQuery(id+"F0.wireOp",EDGE,"E11")])],"isStart":true});
            extrude(context, id + "F46", {"entities" : qUnion([Q0, Q1, Q2, Q3, Q4, Q5]), "operationType" : NewBodyOperationType.REMOVE, "endBound" : BoundingType.UP_TO_SURFACE, "oppositeDirection" : true, "endBoundEntityFace" : qUnion([Q6]), "depth" : 25.4 * mm});
        }
    });
